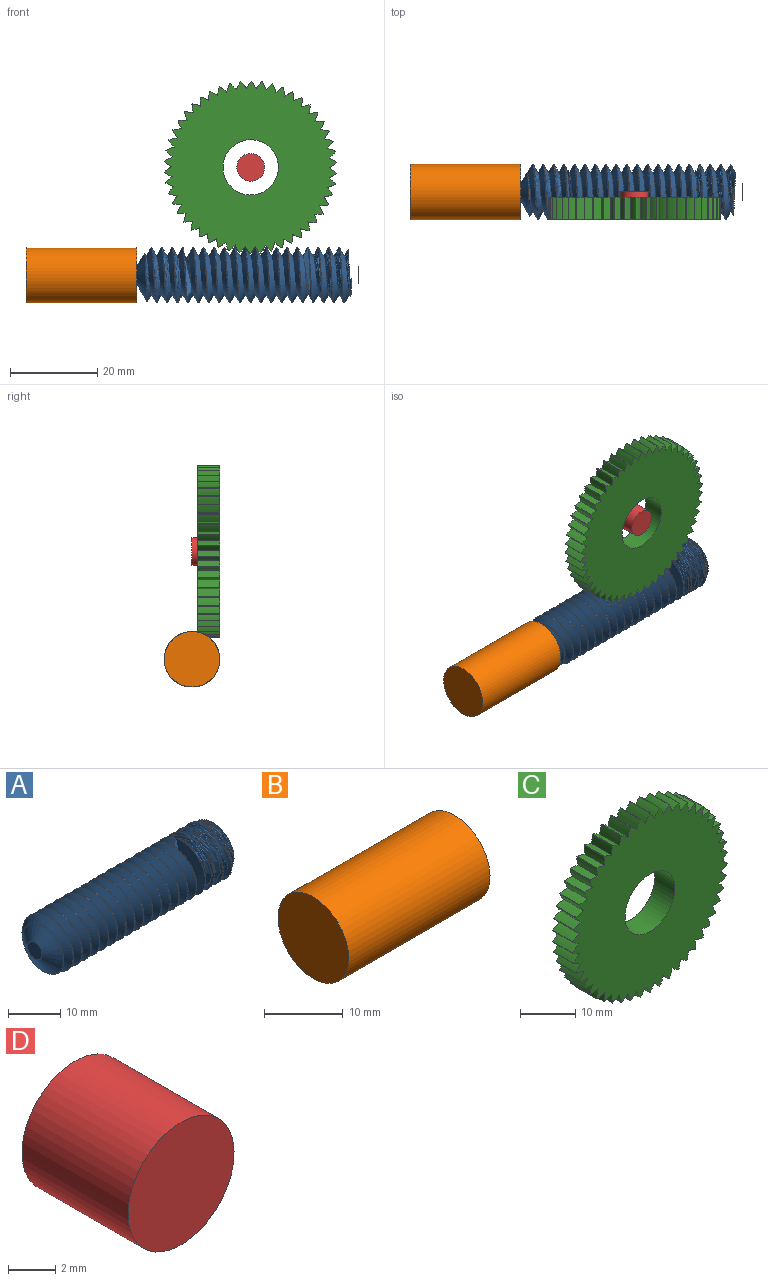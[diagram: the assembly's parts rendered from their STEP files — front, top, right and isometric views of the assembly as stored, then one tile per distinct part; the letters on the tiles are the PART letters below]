
ASSEMBLY  parts=4 mates=2
PART A: 7 faces, bbox 50.8x12.7x14.7 mm
  f0: cylinder r=6.35mm len=45.72mm, axis (-1,0,0), area 336.7mm2, adj f3,f4,f5,f6
  f1: plane 3.9x3.9mm, normal (1,0,0), area 12mm2, adj f3
  f2: plane 3.9x3.9mm, normal (-1,0,0), area 12mm2, adj f4
  f3: cone r=1.95mm half-angle=60deg, axis (-1,0,0), area 93.5mm2, adj f0,f1,f5,f6
  f4: cone r=6.35mm half-angle=60deg, axis (1,0,0), area 93.6mm2, adj f0,f2,f5,f6
  f5: bspline ~49.42x14.66mm, area 1508.2mm2, adj f0,f3,f4,f6
  f6: bspline ~49.42x14.66mm, area 1513.4mm2, adj f0,f3,f4,f5
PART B: 3 faces, bbox 25.4x12.7x12.7 mm
  f0: cylinder r=6.35mm len=25.4mm, axis (1,0,0), area 1013.4mm2, adj f1,f2
  f1: plane 12.7x12.7mm, normal (-1,0,0), area 126.7mm2, adj f0
  f2: plane 12.7x12.7mm, normal (1,0,0), area 126.7mm2, adj f0
PART C: 153 faces, bbox 39.6x5.1x39.6 mm
  f0: cylinder r=19.81mm len=5.08mm, axis (0,1,0), area 0.5mm2, adj f49,f52,f53,f152
  f1: cylinder r=19.81mm len=5.08mm, axis (0,1,0), area 0.5mm2, adj f49,f52,f150,f151
  f2: cylinder r=19.81mm len=5.08mm, axis (0,1,0), area 0.5mm2, adj f49,f52,f148,f149
  f3: cylinder r=19.81mm len=5.08mm, axis (0,1,0), area 0.5mm2, adj f49,f52,f146,f147
  f4: cylinder r=19.81mm len=5.08mm, axis (0,1,0), area 0.5mm2, adj f49,f52,f137,f144
  f5: cylinder r=19.81mm len=5.08mm, axis (0,1,0), area 0.5mm2, adj f49,f52,f142,f143
  f6: cylinder r=19.81mm len=5.08mm, axis (0,1,0), area 0.5mm2, adj f49,f52,f140,f145
  f7: cylinder r=19.81mm len=5.08mm, axis (0,1,0), area 0.5mm2, adj f49,f52,f138,f139
  f8: cylinder r=19.81mm len=5.08mm, axis (0,1,0), area 0.5mm2, adj f49,f52,f136,f141
  f9: cylinder r=19.81mm len=5.08mm, axis (0,1,0), area 0.5mm2, adj f49,f52,f134,f135
  f10: cylinder r=19.81mm len=5.08mm, axis (0,1,0), area 0.5mm2, adj f49,f52,f132,f133
  f11: cylinder r=19.81mm len=5.08mm, axis (0,1,0), area 0.5mm2, adj f49,f52,f130,f131
  f12: cylinder r=19.81mm len=5.08mm, axis (0,1,0), area 0.5mm2, adj f49,f52,f128,f129
  f13: cylinder r=19.81mm len=5.08mm, axis (0,1,0), area 0.5mm2, adj f49,f52,f126,f127
  f14: cylinder r=19.81mm len=5.08mm, axis (0,1,0), area 0.5mm2, adj f49,f52,f124,f125
  f15: cylinder r=19.81mm len=5.08mm, axis (0,1,0), area 0.5mm2, adj f49,f52,f122,f123
  f16: cylinder r=19.81mm len=5.08mm, axis (0,1,0), area 0.5mm2, adj f49,f52,f113,f120
  f17: cylinder r=19.81mm len=5.08mm, axis (0,1,0), area 0.5mm2, adj f49,f52,f118,f119
  f18: cylinder r=19.81mm len=5.08mm, axis (0,1,0), area 0.5mm2, adj f49,f52,f116,f121
  f19: cylinder r=19.81mm len=5.08mm, axis (0,1,0), area 0.5mm2, adj f49,f52,f114,f115
  f20: cylinder r=19.81mm len=5.08mm, axis (0,1,0), area 0.5mm2, adj f49,f52,f112,f117
  f21: cylinder r=19.81mm len=5.08mm, axis (0,1,0), area 0.5mm2, adj f49,f52,f110,f111
  f22: cylinder r=19.81mm len=5.08mm, axis (0,1,0), area 0.5mm2, adj f49,f52,f108,f109
  f23: cylinder r=19.81mm len=5.08mm, axis (0,1,0), area 0.5mm2, adj f49,f52,f106,f107
  f24: cylinder r=19.81mm len=5.08mm, axis (0,1,0), area 0.5mm2, adj f49,f52,f104,f105
  f25: cylinder r=19.81mm len=5.08mm, axis (0,1,0), area 0.5mm2, adj f49,f52,f102,f103
  f26: cylinder r=19.81mm len=5.08mm, axis (0,1,0), area 0.5mm2, adj f49,f52,f100,f101
  f27: cylinder r=19.81mm len=5.08mm, axis (0,1,0), area 0.5mm2, adj f49,f52,f98,f99
  f28: cylinder r=19.81mm len=5.08mm, axis (0,1,0), area 0.5mm2, adj f49,f52,f91,f96
  f29: cylinder r=19.81mm len=5.08mm, axis (0,1,0), area 0.5mm2, adj f49,f52,f94,f95
  f30: cylinder r=19.81mm len=5.08mm, axis (0,1,0), area 0.5mm2, adj f49,f52,f89,f92
  f31: cylinder r=19.81mm len=5.08mm, axis (0,1,0), area 0.5mm2, adj f49,f52,f90,f97
  f32: cylinder r=19.81mm len=5.08mm, axis (0,1,0), area 0.5mm2, adj f49,f52,f88,f93
  f33: cylinder r=19.81mm len=5.08mm, axis (0,1,0), area 0.5mm2, adj f49,f52,f86,f87
  f34: cylinder r=19.81mm len=5.08mm, axis (0,1,0), area 0.5mm2, adj f49,f52,f84,f85
  f35: cylinder r=19.81mm len=5.08mm, axis (0,1,0), area 0.5mm2, adj f49,f52,f82,f83
  f36: cylinder r=19.81mm len=5.08mm, axis (0,1,0), area 0.5mm2, adj f49,f52,f80,f81
  f37: cylinder r=19.81mm len=5.08mm, axis (0,1,0), area 0.5mm2, adj f49,f52,f78,f79
  f38: cylinder r=19.81mm len=5.08mm, axis (0,1,0), area 0.5mm2, adj f49,f52,f76,f77
  f39: cylinder r=19.81mm len=5.08mm, axis (0,1,0), area 0.5mm2, adj f49,f52,f74,f75
  f40: cylinder r=19.81mm len=5.08mm, axis (0,1,0), area 0.5mm2, adj f49,f52,f69,f72
  f41: cylinder r=19.81mm len=5.08mm, axis (0,1,0), area 0.5mm2, adj f49,f52,f67,f70
  f42: cylinder r=19.81mm len=5.08mm, axis (0,1,0), area 0.5mm2, adj f49,f52,f65,f68
  f43: cylinder r=19.81mm len=5.08mm, axis (0,1,0), area 0.5mm2, adj f49,f52,f59,f66
  f44: cylinder r=19.81mm len=5.08mm, axis (0,1,0), area 0.5mm2, adj f49,f52,f64,f73
  f45: cylinder r=19.81mm len=5.08mm, axis (0,1,0), area 0.5mm2, adj f49,f52,f62,f63
  f46: cylinder r=19.81mm len=5.08mm, axis (0,1,0), area 0.5mm2, adj f49,f52,f57,f60
  f47: cylinder r=19.81mm len=5.08mm, axis (0,1,0), area 0.5mm2, adj f49,f52,f58,f61
  f48: cylinder r=19.81mm len=5.08mm, axis (0,1,0), area 0.5mm2, adj f49,f52,f56,f71
  f49: plane 39.63x39.55mm, normal (0,-1,0), area 1012.4mm2, adj f0,f1,f2,f3,f4,f5,f6,f7
  f50: cylinder r=6.35mm len=12.7mm, axis (0,1,0), area 202.7mm2, adj f49,f52
  f51: cylinder r=19.81mm len=5.08mm, axis (0,1,0), area 0.5mm2, adj f49,f52,f54,f55
  f52: plane 39.63x39.55mm, normal (0,1,0), area 1012.4mm2, adj f0,f1,f2,f3,f4,f5,f6,f7
  f53: extruded ~5.08x1.63mm, area 10.3mm2, adj f0,f49,f52,f54
  f54: extruded ~5.08x1.63mm, area 10.3mm2, adj f49,f51,f52,f53
  f55: extruded ~5.08x1.77mm, area 10.3mm2, adj f49,f51,f52,f56
  f56: extruded ~5.08x1.46mm, area 10.3mm2, adj f48,f49,f52,f55
  f57: extruded ~5.08x1.96mm, area 10.3mm2, adj f46,f49,f52,f58
  f58: extruded ~5.08x2.02mm, area 10.3mm2, adj f47,f49,f52,f57
  f59: extruded ~5.08x2.01mm, area 10.3mm2, adj f43,f49,f52,f60
  f60: extruded ~5.08x1.99mm, area 10.3mm2, adj f46,f49,f52,f59
  f61: extruded ~5.08x1.89mm, area 10.3mm2, adj f47,f49,f52,f62
  f62: extruded ~5.08x2.02mm, area 10.3mm2, adj f45,f49,f52,f61
  f63: extruded ~5.08x1.78mm, area 10.3mm2, adj f45,f49,f52,f64
  f64: extruded ~5.08x1.98mm, area 10.3mm2, adj f44,f49,f52,f63
  f65: extruded ~5.08x2.02mm, area 10.3mm2, adj f42,f49,f52,f66
  f66: extruded ~5.08x1.93mm, area 10.3mm2, adj f43,f49,f52,f65
  f67: extruded ~5.08x2mm, area 10.3mm2, adj f41,f49,f52,f68
  f68: extruded ~5.08x1.84mm, area 10.3mm2, adj f42,f49,f52,f67
  f69: extruded ~5.08x1.96mm, area 10.3mm2, adj f40,f49,f52,f70
  f70: extruded ~5.08x1.71mm, area 10.3mm2, adj f41,f49,f52,f69
  f71: extruded ~5.08x1.88mm, area 10.3mm2, adj f48,f49,f52,f72
  f72: extruded ~5.08x1.57mm, area 10.3mm2, adj f40,f49,f52,f71
  f73: extruded ~5.08x1.64mm, area 10.3mm2, adj f44,f49,f52,f74
  f74: extruded ~5.08x1.92mm, area 10.3mm2, adj f39,f49,f52,f73
  f75: extruded ~5.08x1.48mm, area 10.3mm2, adj f39,f49,f52,f76
  f76: extruded ~5.08x1.82mm, area 10.3mm2, adj f38,f49,f52,f75
  f77: extruded ~5.08x1.55mm, area 10.3mm2, adj f38,f49,f52,f78
  f78: extruded ~5.08x1.7mm, area 10.3mm2, adj f37,f49,f52,f77
  f79: extruded ~5.08x1.7mm, area 10.3mm2, adj f37,f49,f52,f80
  f80: extruded ~5.08x1.55mm, area 10.3mm2, adj f36,f49,f52,f79
  f81: extruded ~5.08x1.82mm, area 10.3mm2, adj f36,f49,f52,f82
  f82: extruded ~5.08x1.48mm, area 10.3mm2, adj f35,f49,f52,f81
  f83: extruded ~5.08x1.92mm, area 10.3mm2, adj f35,f49,f52,f84
  f84: extruded ~5.08x1.64mm, area 10.3mm2, adj f34,f49,f52,f83
  f85: extruded ~5.08x1.98mm, area 10.3mm2, adj f34,f49,f52,f86
  f86: extruded ~5.08x1.78mm, area 10.3mm2, adj f33,f49,f52,f85
  f87: extruded ~5.08x2.02mm, area 10.3mm2, adj f33,f49,f52,f88
  f88: extruded ~5.08x1.89mm, area 10.3mm2, adj f32,f49,f52,f87
  f89: extruded ~5.08x1.84mm, area 10.3mm2, adj f30,f49,f52,f90
  f90: extruded ~5.08x2mm, area 10.3mm2, adj f31,f49,f52,f89
  f91: extruded ~5.08x1.93mm, area 10.3mm2, adj f28,f49,f52,f92
  f92: extruded ~5.08x2.02mm, area 10.3mm2, adj f30,f49,f52,f91
  f93: extruded ~5.08x2.02mm, area 10.3mm2, adj f32,f49,f52,f94
  f94: extruded ~5.08x1.96mm, area 10.3mm2, adj f29,f49,f52,f93
  f95: extruded ~5.08x1.99mm, area 10.3mm2, adj f29,f49,f52,f96
  f96: extruded ~5.08x2.01mm, area 10.3mm2, adj f28,f49,f52,f95
  f97: extruded ~5.08x1.71mm, area 10.3mm2, adj f31,f49,f52,f98
  f98: extruded ~5.08x1.96mm, area 10.3mm2, adj f27,f49,f52,f97
  f99: extruded ~5.08x1.57mm, area 10.3mm2, adj f27,f49,f52,f100
  f100: extruded ~5.08x1.88mm, area 10.3mm2, adj f26,f49,f52,f99
  f101: extruded ~5.08x1.46mm, area 10.3mm2, adj f26,f49,f52,f102
  f102: extruded ~5.08x1.77mm, area 10.3mm2, adj f25,f49,f52,f101
  f103: extruded ~5.08x1.63mm, area 10.3mm2, adj f25,f49,f52,f104
  f104: extruded ~5.08x1.63mm, area 10.3mm2, adj f24,f49,f52,f103
  f105: extruded ~5.08x1.77mm, area 10.3mm2, adj f24,f49,f52,f106
  f106: extruded ~5.08x1.46mm, area 10.3mm2, adj f23,f49,f52,f105
  f107: extruded ~5.08x1.88mm, area 10.3mm2, adj f23,f49,f52,f108
  f108: extruded ~5.08x1.57mm, area 10.3mm2, adj f22,f49,f52,f107
  f109: extruded ~5.08x1.96mm, area 10.3mm2, adj f22,f49,f52,f110
  f110: extruded ~5.08x1.71mm, area 10.3mm2, adj f21,f49,f52,f109
  f111: extruded ~5.08x2mm, area 10.3mm2, adj f21,f49,f52,f112
  f112: extruded ~5.08x1.84mm, area 10.3mm2, adj f20,f49,f52,f111
  f113: extruded ~5.08x1.96mm, area 10.3mm2, adj f16,f49,f52,f114
  f114: extruded ~5.08x2.02mm, area 10.3mm2, adj f19,f49,f52,f113
  f115: extruded ~5.08x1.89mm, area 10.3mm2, adj f19,f49,f52,f116
  f116: extruded ~5.08x2.02mm, area 10.3mm2, adj f18,f49,f52,f115
  f117: extruded ~5.08x2.02mm, area 10.3mm2, adj f20,f49,f52,f118
  f118: extruded ~5.08x1.93mm, area 10.3mm2, adj f17,f49,f52,f117
  f119: extruded ~5.08x2.01mm, area 10.3mm2, adj f17,f49,f52,f120
  f120: extruded ~5.08x1.99mm, area 10.3mm2, adj f16,f49,f52,f119
  f121: extruded ~5.08x1.78mm, area 10.3mm2, adj f18,f49,f52,f122
  f122: extruded ~5.08x1.98mm, area 10.3mm2, adj f15,f49,f52,f121
  f123: extruded ~5.08x1.64mm, area 10.3mm2, adj f15,f49,f52,f124
  f124: extruded ~5.08x1.92mm, area 10.3mm2, adj f14,f49,f52,f123
  f125: extruded ~5.08x1.48mm, area 10.3mm2, adj f14,f49,f52,f126
  f126: extruded ~5.08x1.82mm, area 10.3mm2, adj f13,f49,f52,f125
  f127: extruded ~5.08x1.55mm, area 10.3mm2, adj f13,f49,f52,f128
  f128: extruded ~5.08x1.7mm, area 10.3mm2, adj f12,f49,f52,f127
  f129: extruded ~5.08x1.7mm, area 10.3mm2, adj f12,f49,f52,f130
  f130: extruded ~5.08x1.55mm, area 10.3mm2, adj f11,f49,f52,f129
  f131: extruded ~5.08x1.82mm, area 10.3mm2, adj f11,f49,f52,f132
  f132: extruded ~5.08x1.48mm, area 10.3mm2, adj f10,f49,f52,f131
  f133: extruded ~5.08x1.92mm, area 10.3mm2, adj f10,f49,f52,f134
  f134: extruded ~5.08x1.64mm, area 10.3mm2, adj f9,f49,f52,f133
  f135: extruded ~5.08x1.98mm, area 10.3mm2, adj f9,f49,f52,f136
  f136: extruded ~5.08x1.78mm, area 10.3mm2, adj f8,f49,f52,f135
  f137: extruded ~5.08x1.99mm, area 10.3mm2, adj f4,f49,f52,f138
  f138: extruded ~5.08x2.01mm, area 10.3mm2, adj f7,f49,f52,f137
  f139: extruded ~5.08x1.93mm, area 10.3mm2, adj f7,f49,f52,f140
  f140: extruded ~5.08x2.02mm, area 10.3mm2, adj f6,f49,f52,f139
  f141: extruded ~5.08x2.02mm, area 10.3mm2, adj f8,f49,f52,f142
  f142: extruded ~5.08x1.89mm, area 10.3mm2, adj f5,f49,f52,f141
  f143: extruded ~5.08x2.02mm, area 10.3mm2, adj f5,f49,f52,f144
  f144: extruded ~5.08x1.96mm, area 10.3mm2, adj f4,f49,f52,f143
  f145: extruded ~5.08x1.84mm, area 10.3mm2, adj f6,f49,f52,f146
  f146: extruded ~5.08x2mm, area 10.3mm2, adj f3,f49,f52,f145
  f147: extruded ~5.08x1.71mm, area 10.3mm2, adj f3,f49,f52,f148
  f148: extruded ~5.08x1.96mm, area 10.3mm2, adj f2,f49,f52,f147
  f149: extruded ~5.08x1.57mm, area 10.3mm2, adj f2,f49,f52,f150
  f150: extruded ~5.08x1.88mm, area 10.3mm2, adj f1,f49,f52,f149
  f151: extruded ~5.08x1.46mm, area 10.3mm2, adj f1,f49,f52,f152
  f152: extruded ~5.08x1.77mm, area 10.3mm2, adj f0,f49,f52,f151
PART D: 3 faces, bbox 6.4x6.4x6.4 mm
  f0: cylinder r=3.17mm len=6.35mm, axis (0,1,0), area 126.7mm2, adj f1,f2
  f1: plane 6.35x6.35mm, normal (0,-1,0), area 31.7mm2, adj f0
  f2: plane 6.35x6.35mm, normal (0,1,0), area 31.7mm2, adj f0
PLACE A rot(axis=(1,0,0),19.6deg) t=(0,0,0)mm
PLACE B at identity fixed
PLACE C rot(axis=(0,1,0),29.2deg) t=(-8.75,-1.27,15.91)mm
PLACE D at identity fixed
MATE revolute C.f0 <-> D.f0  axis (0,-1,0) through (26.18,-6.35,24.76)mm
MATE revolute A.f0 <-> B.f0  axis (-1,0,0) through (0,0,0)mm
